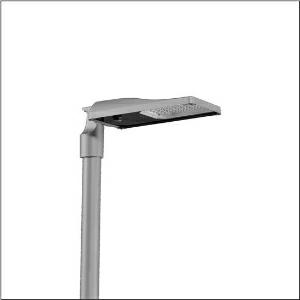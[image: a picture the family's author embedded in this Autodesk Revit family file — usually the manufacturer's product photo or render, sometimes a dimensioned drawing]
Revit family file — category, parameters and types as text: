
# Revit family: streetlight_sl_31_mini___st1_0a_5xh6d31r08ja_5198
name_source: partatom
category: Lighting Fixtures
units: mm (PartAtom-declared; Revit-internal decimal feet)

## family parameters
Cut with Voids When Loaded = No
Host = Face
Light Source = No
Part Type = Normal
Room Calculation Point = No
Round Connector Dimension = Use Diameter
Shared = No

## types (1)
- --- (1 x LED, 12270 lm, 82.5 W, 3000K)
    Apparent Load = 83 VA
    CIE Flux Codes = 40 73 97 100 100
    Color Rendering = 70
    Color Temperature = 3000K
    Default Elevation = 1800 mm
    Description = Streetlight SL 31 mini D4i, Desk-Remote mast luminaire for post-top, side-entry; light control with lens of PMMA; light distribution: ST1.0a, direct asymmetric distribution, for standard-compliant lighting for roads and squares; LED: luminous flux: 12.270lm, light colour: 730, colour temperature: 3000K; luminous efficacy: 148,7lm/W; control: pre-setting: logarithmic dimming characteristic, flexible luminous flux parameterisation, time-dependent luminous flux control, constant luminous flux control, power reduction, intelligent temperature release in ECG and LED module, overheat protection; luminaire housing, of diecast aluminium, Siteco® metallic grey (DB 702S), corrosivity category C5 high according to DIN EN ISO 12944; cover of toughened safety glass, transparent, opened without tools; mast flange of diecast aluminium, Siteco® metallic grey (DB 702S), spigot size: 76/60mm, mast flange included unmounted; with cable H07RN-F 2x 1.5mm², cable length: 10,5m, connection cable pre-assembled; mains connection: 220..240V, AC, 50/60Hz; power consumption (at start of service life): 82,5W / (at end of service life): 90,1W / (with reduced operation 50%): 36,8W; protection rating (complete): IP66; insulation class (complete): insulation class II (safety insulation); impact resistance: IK09; certification: CE, ENEC, ENEC+, VDE, UKCA, ZD4i; permissible operating ambient temperature for outdoor applications: -40..+50°C; packaging unit: 1 piece

Light Distribution: ST1.0a
    Height = 76 mm
    Lamp = 1 x LED
    Lamp Light Flux = 12270 lm
    Lamp Power = 82.5 W
    Lamp count = 1
    Length = 547 mm
    Luminous efficacy = 149 lm/W
    Manufacturer = Siteco
    ModVariant = No
    Model = 5XH6D31R08JA
    Number of Poles = 1
    OnlyDefault = Yes
    Power Factor = 1
    Product Name = Streetlight SL 31 mini | ST1.0a
    Product group = mast luminaire | pylon top
    ProductGroupID = 6100
    Protection Class = Protection class II
    Protection Degree = IP 66
    RLX_Detail_Level = 1
    RLX_Emergency_Light_Flux = 0 lm
    RLX_Emergency_Type = 0
    RLX_Emergency_Type_DB = No
    RlxData = <blob elided: 39785 chars, md5=82171fa4>
    Socket = socket
    Standby Power = 0 W
    System Light Flux = 12270 lm
    System Power = 83 W
    Type Comments = factory setting: luminous flux: 100 % | dim-lin: 254 | 870 mA
    Type Image = l_1300328.jpg
    URL = http://relux.com
    VarID = @adj_070917
    Voltage = 0 V
    Weight = 0.00 kg
    Width = 265 mm

## geometry (parser evidence)
native form markers: Blend x4, Sweep x9
no freeform markers — native parametric forms only
